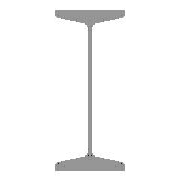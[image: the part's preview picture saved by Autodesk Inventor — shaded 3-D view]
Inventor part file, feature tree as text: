
AUTODESK INVENTOR PART (.ipt)
format: ipt  version: 2025 (Build 290162010, 162A)  size: 171,008 bytes
history: native  units: mm (DEFAULTED — no unit token found)
features: other x3, sketch x1, plane x1
ambient origin geometry x8: Origin, YZ Plane, XZ Plane, XY Plane, X Axis, Y Axis, Z Axis, Center Point
bodies: Solid1 (feature_tree), Body (feature_tree)
feature tree (5):
  other  "Driven Length"
  other  "Start plane"
  other  "End plane"
  sketch  "Sketch3"  dims[d1=3.94217mm d2=12.0mm d3=28.05mm d4=3.9mm d5=60.0mm d6=6000.0mm d7=0.0mm d10=120.0mm d14=6.0mm d15=12.0mm d16=-0.0mm d17=6000.0mm d18=90.0deg d19=6000.0mm]
  plane  "Work Plane3"
